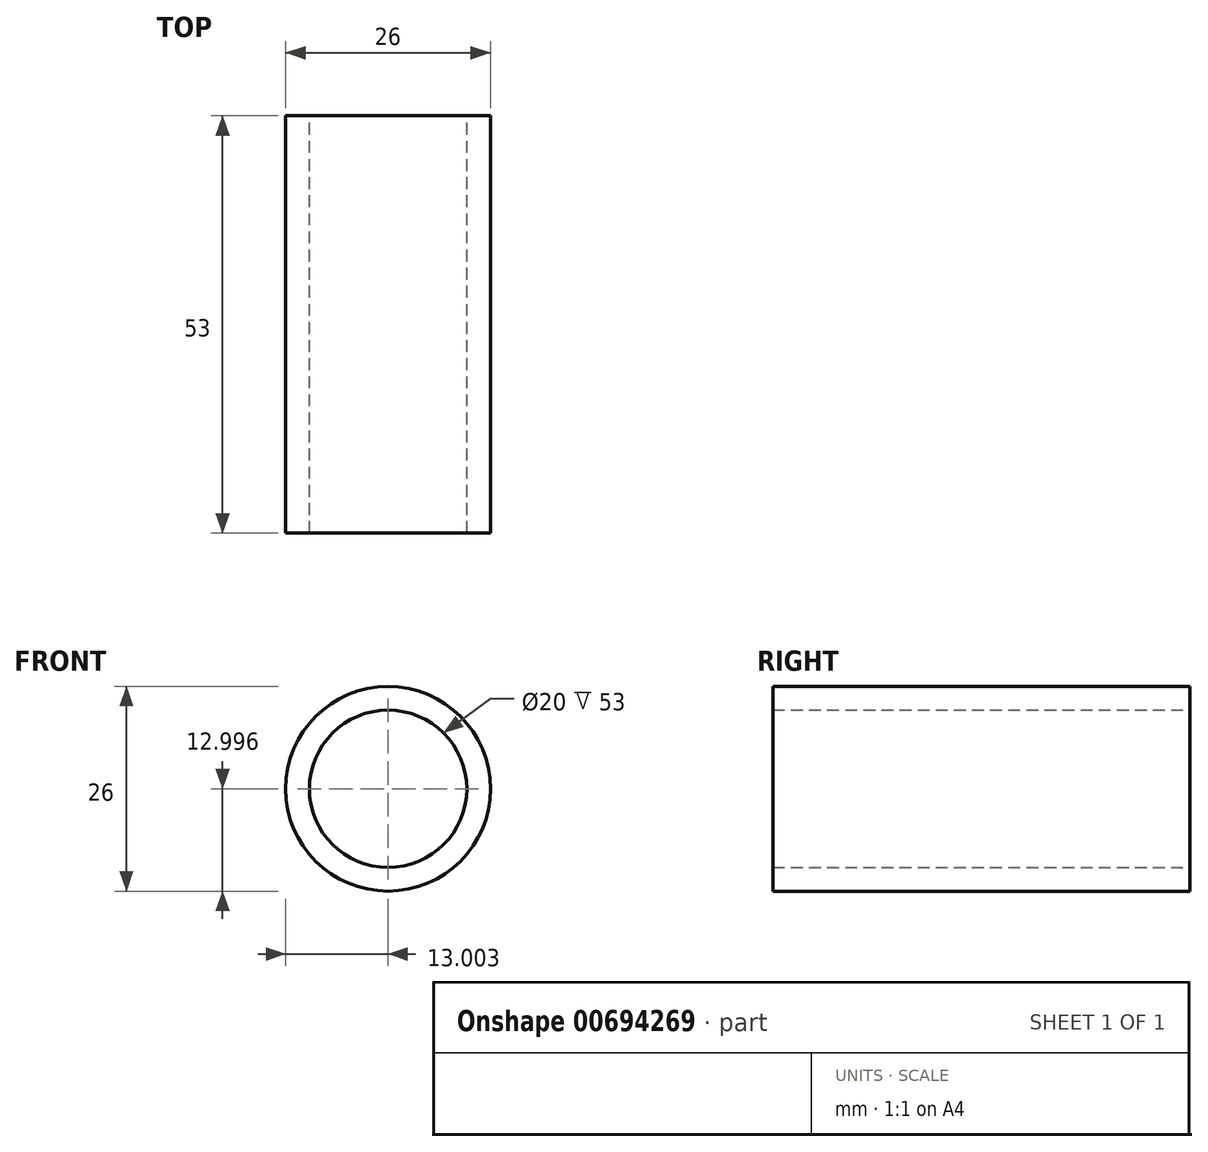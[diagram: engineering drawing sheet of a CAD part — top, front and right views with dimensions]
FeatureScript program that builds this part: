
annotation { "Feature Type Name" : "Feature", "Feature Type Description" : "" }
export const myFeature = defineFeature(function(context is Context, id is Id, definition is map)
    precondition{}
    {
        {
            var Q0;
            Q0=qCreatedBy(makeId("Front.planeOp"),FACE);
            var sketch = newSketch(context, id + "F0", { "sketchPlane" : qUnion([Q0])});
            skCircle(sketch, "E0", {"center": v(0.15, -0.61) * mm, "radius": 10 * mm});
            skCircle(sketch, "E1", {"center": v(0.15, -0.61) * mm, "radius": 13 * mm});
            skSolve(sketch);
        }
        {
            var Q0;
            Q0=qSketchRegion(id+"F0",true);
            extrude(context, id + "F1", {"entities" : qUnion([Q0]), "depth" : (20 + 33) * mm, "offsetDistance" : 25 * mm});
        }
    });
